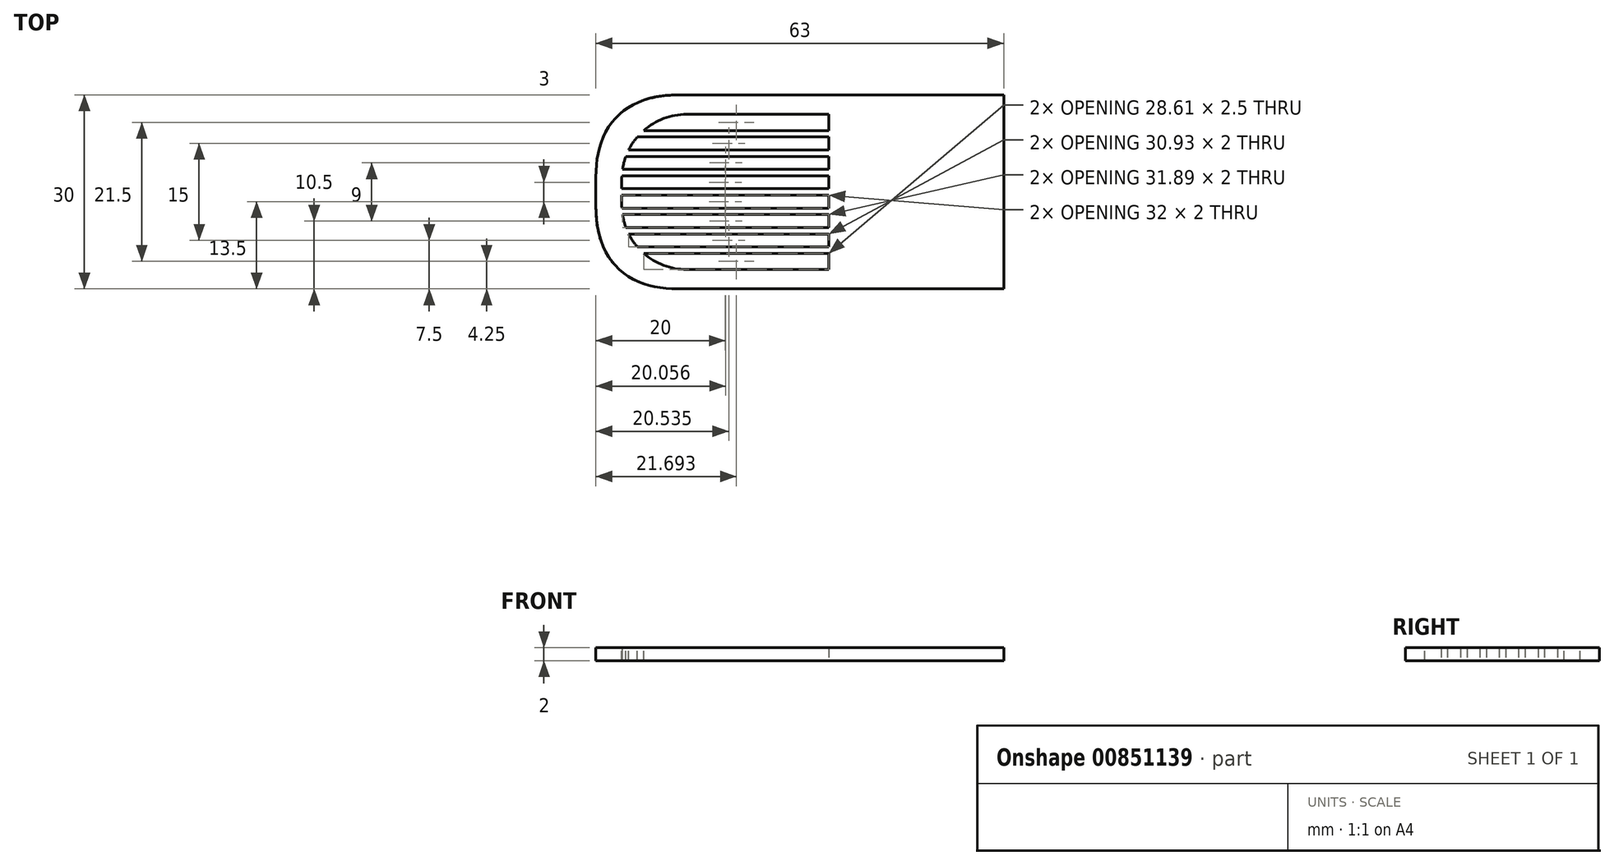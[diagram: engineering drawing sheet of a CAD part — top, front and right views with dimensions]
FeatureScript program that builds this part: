
annotation { "Feature Type Name" : "Feature", "Feature Type Description" : "" }
export const myFeature = defineFeature(function(context is Context, id is Id, definition is map)
    precondition{}
    {
        {
            var Q0;
            Q0=qCreatedBy(makeId("Top.planeOp"),FACE);
            var sketch = newSketch(context, id + "F0", { "sketchPlane" : qUnion([Q0])});
            skLineSegment(sketch, "E0.bottom", {"start": v(-31.5, 15) * mm, "end": v(31.5, 15) * mm});
            skLineSegment(sketch, "E0.top", {"start": v(-31.5, -15) * mm, "end": v(31.5, -15) * mm});
            skLineSegment(sketch, "E0.left", {"start": v(-31.5, 15) * mm, "end": v(-31.5, -15) * mm});
            skLineSegment(sketch, "E0.right", {"start": v(31.5, 15) * mm, "end": v(31.5, -15) * mm});
            skPoint(sketch, "E0.middle", {"position": v(0, 0) * mm});
            skSolve(sketch);
        }
        {
            var Q0;
            Q0=makeQuery(id+"F0.imprint","IMPRINT",FACE,{"disambiguationData":[TD([[makeQuery(id+"F0.imprint","IMPRINT",EDGE,{"derivedFrom":sQuery(id+"F0.wireOp",EDGE,"E0.bottom")}),-1.0]])]});
            extrude(context, id + "F1", {"entities" : qUnion([Q0]), "depth" : 2 * mm, "offsetDistance" : 25 * mm});
        }
        {
            var Q0;
            Q0=makeQuery(id+"F1.opExtrude","SWEPT_EDGE",EDGE,{"disambiguationData":[OSD([sQuery(id+"F0.wireOp",EDGE,"E0.bottom"),sQuery(id+"F0.wireOp",EDGE,"E0.left")])]});
            var Q1;
            Q1=makeQuery(id+"F1.opExtrude","SWEPT_EDGE",EDGE,{"disambiguationData":[OSD([sQuery(id+"F0.wireOp",EDGE,"E0.top"),sQuery(id+"F0.wireOp",EDGE,"E0.left")])]});
            fillet(context, id + "F2", {"entities" : qUnion([Q0, Q1]), "radius" : 12.7 * mm, "tangentPropagation" : true, "rho" : 0.48, "crossSection" : FilletCrossSection.CONIC, "allowEdgeOverflow" : false});
        }
        {
            var Q0;
            Q0=makeQuery(id+"F1.opExtrude","CAP_FACE",FACE,{"disambiguationData":[OSD([sQuery(id+"F0.wireOp",EDGE,"E0.bottom"),sQuery(id+"F0.wireOp",EDGE,"E0.top"),sQuery(id+"F0.wireOp",EDGE,"E0.left"),sQuery(id+"F0.wireOp",EDGE,"E0.right")])],"isStart":false});
            var sketch = newSketch(context, id + "F3", { "sketchPlane" : qUnion([Q0])});
            skLineSegment(sketch, "E1.bottom", {"start": v(-27.5, 12) * mm, "end": v(4.5, 12) * mm});
            skLineSegment(sketch, "E1.top", {"start": v(-27.5, -12) * mm, "end": v(4.5, -12) * mm});
            skLineSegment(sketch, "E1.left", {"start": v(-27.5, 12) * mm, "end": v(-27.5, -12) * mm});
            skLineSegment(sketch, "E1.right", {"start": v(4.5, 12) * mm, "end": v(4.5, -12) * mm});
            skPoint(sketch, "E1.middle", {"position": v(-11.5, 0) * mm});
            skSolve(sketch);
        }
        {
            var Q0;
            Q0=makeQuery(id+"F3.imprint","IMPRINT",FACE,{"disambiguationData":[TD([[makeQuery(id+"F3.imprint","IMPRINT",EDGE,{"derivedFrom":sQuery(id+"F3.wireOp",EDGE,"E1.bottom")}),-1.0]])]});
            extrude(context, id + "F4", {"entities" : qUnion([Q0]), "operationType" : NewBodyOperationType.REMOVE, "oppositeDirection" : true, "depth" : 25 * mm, "offsetDistance" : 25 * mm});
        }
        {
            var Q0;
            Q0=makeQuery(id+"F4.boolean.opBoolean","COPY",EDGE,{"derivedFrom":makeQuery(id+"F4.opExtrude","SWEPT_EDGE",EDGE,{"disambiguationData":[OSD([sQuery(id+"F3.wireOp",EDGE,"E1.bottom"),sQuery(id+"F3.wireOp",EDGE,"E1.left")])]})});
            var Q1;
            Q1=makeQuery(id+"F4.boolean.opBoolean","COPY",EDGE,{"derivedFrom":makeQuery(id+"F4.opExtrude","SWEPT_EDGE",EDGE,{"disambiguationData":[OSD([sQuery(id+"F3.wireOp",EDGE,"E1.top"),sQuery(id+"F3.wireOp",EDGE,"E1.left")])]})});
            fillet(context, id + "F5", {"entities" : qUnion([Q0, Q1]), "radius" : 10 * mm, "tangentPropagation" : true, "allowEdgeOverflow" : false});
        }
        {
            var Q0;
            Q0=makeQuery(id+"F1.opExtrude","CAP_FACE",FACE,{"disambiguationData":[OSD([sQuery(id+"F0.wireOp",EDGE,"E0.bottom"),sQuery(id+"F0.wireOp",EDGE,"E0.top"),sQuery(id+"F0.wireOp",EDGE,"E0.left"),sQuery(id+"F0.wireOp",EDGE,"E0.right")])],"isStart":false});
            var sketch = newSketch(context, id + "F6", { "sketchPlane" : qUnion([Q0])});
            skLineSegment(sketch, "E2", {"start": v(4.5, -9) * mm, "end": v(-28, -9) * mm});
            skLineSegment(sketch, "E3.0.1.0", {"start": v(4.5, -6) * mm, "end": v(-28, -6) * mm});
            skLineSegment(sketch, "E3.0.2.0", {"start": v(4.5, -3) * mm, "end": v(-28, -3) * mm});
            skLineSegment(sketch, "E3.0.3.0", {"start": v(4.5, 0) * mm, "end": v(-28, 0) * mm});
            skLineSegment(sketch, "E3.0.4.0", {"start": v(4.5, 3) * mm, "end": v(-28, 3) * mm});
            skLineSegment(sketch, "E3.0.5.0", {"start": v(4.5, 6) * mm, "end": v(-28, 6) * mm});
            skLineSegment(sketch, "E3.0.6.0", {"start": v(4.5, 9) * mm, "end": v(-28, 9) * mm});
            skLineSegment(sketch, "E3.direction1", {"start": v(-28, -9) * mm, "end": v(-3, -9) * mm, "construction": true});
            skLineSegment(sketch, "E3.direction2", {"start": v(-28, -9) * mm, "end": v(-28, -6) * mm, "construction": true});
            skSolve(sketch);
        }
        {
            var Q0;
            Q0=sQuery(id+"F6.wireOp",EDGE,"E2");
            var Q1;
            Q1=sQuery(id+"F6.wireOp",EDGE,"E3.0.1.0");
            var Q2;
            Q2=sQuery(id+"F6.wireOp",EDGE,"E3.0.2.0");
            var Q3;
            Q3=sQuery(id+"F6.wireOp",EDGE,"E3.0.3.0");
            var Q4;
            Q4=sQuery(id+"F6.wireOp",EDGE,"E3.0.4.0");
            var Q5;
            Q5=sQuery(id+"F6.wireOp",EDGE,"E3.0.5.0");
            var Q6;
            Q6=sQuery(id+"F6.wireOp",EDGE,"E3.0.6.0");
            extrude(context, id + "F7", {"bodyType" : ToolBodyType.SURFACE, "surfaceEntities" : qUnion([Q0, Q1, Q2, Q3, Q4, Q5, Q6]), "oppositeDirection" : true, "depth" : 2 * mm, "offsetDistance" : 25 * mm});
        }
        {
            var Q0;
            Q0=makeQuery(id+"F7.opExtrude","SWEPT_FACE",FACE,{"disambiguationData":[OSD([sQuery(id+"F6.wireOp",EDGE,"E2")])]});
            var Q1;
            Q1=makeQuery(id+"F7.opExtrude","SWEPT_FACE",FACE,{"disambiguationData":[OSD([sQuery(id+"F6.wireOp",EDGE,"E3.0.1.0")])]});
            var Q2;
            Q2=makeQuery(id+"F7.opExtrude","SWEPT_FACE",FACE,{"disambiguationData":[OSD([sQuery(id+"F6.wireOp",EDGE,"E3.0.2.0")])]});
            var Q3;
            Q3=makeQuery(id+"F7.opExtrude","SWEPT_FACE",FACE,{"disambiguationData":[OSD([sQuery(id+"F6.wireOp",EDGE,"E3.0.3.0")])]});
            var Q4;
            Q4=makeQuery(id+"F7.opExtrude","SWEPT_FACE",FACE,{"disambiguationData":[OSD([sQuery(id+"F6.wireOp",EDGE,"E3.0.4.0")])]});
            var Q5;
            Q5=makeQuery(id+"F7.opExtrude","SWEPT_FACE",FACE,{"disambiguationData":[OSD([sQuery(id+"F6.wireOp",EDGE,"E3.0.5.0")])]});
            var Q6;
            Q6=makeQuery(id+"F7.opExtrude","SWEPT_FACE",FACE,{"disambiguationData":[OSD([sQuery(id+"F6.wireOp",EDGE,"E3.0.6.0")])]});
            extrude(context, id + "F8", {"entities" : qUnion([Q0, Q1, Q2, Q3, Q4, Q5, Q6]), "operationType" : NewBodyOperationType.ADD, "endBound" : BoundingType.SYMMETRIC, "depth" : 1 * mm, "offsetDistance" : 25 * mm});
        }
    });
